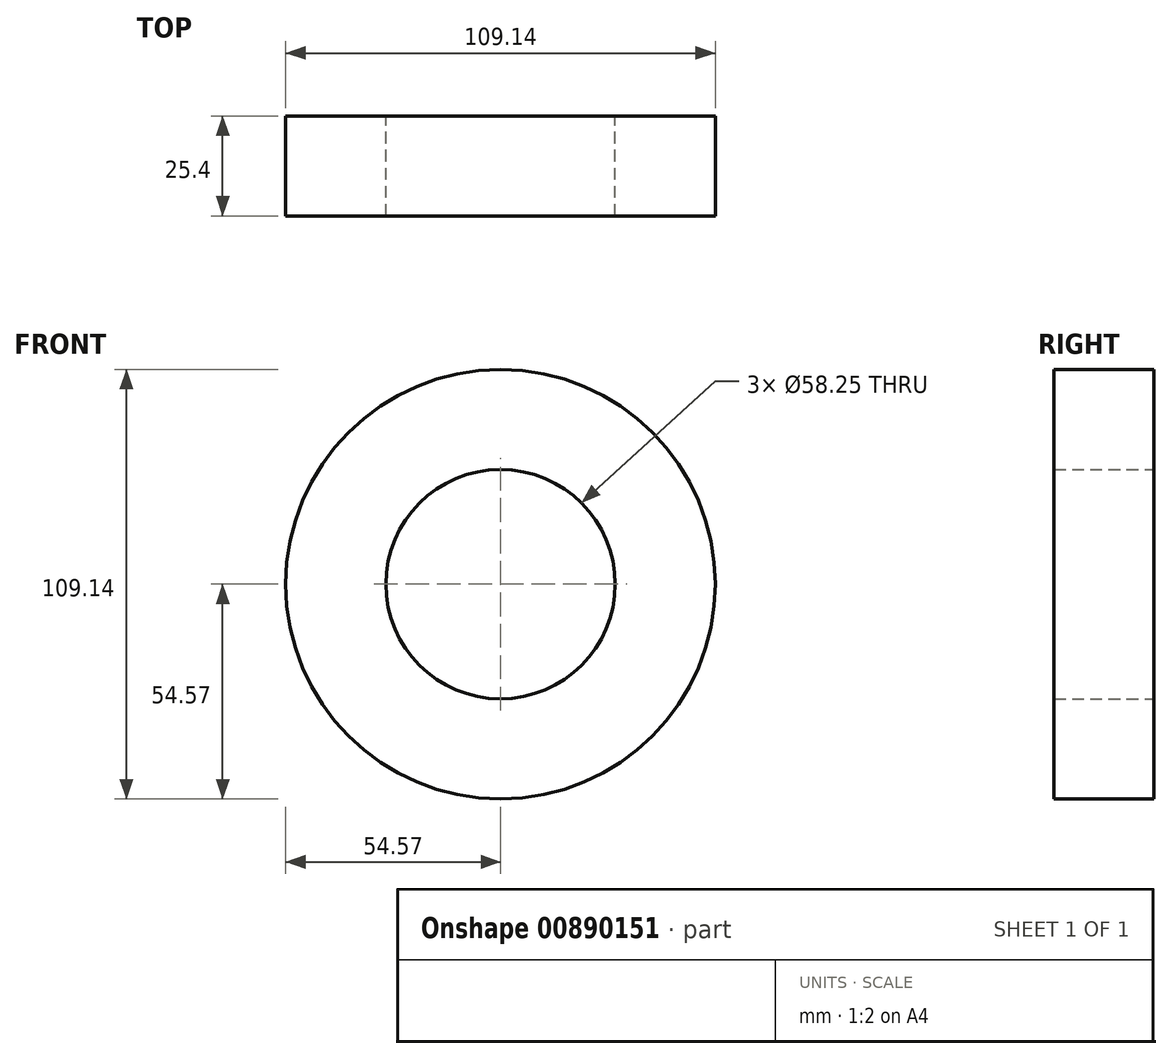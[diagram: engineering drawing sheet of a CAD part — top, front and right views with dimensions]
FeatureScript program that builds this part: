
annotation { "Feature Type Name" : "Feature", "Feature Type Description" : "" }
export const myFeature = defineFeature(function(context is Context, id is Id, definition is map)
    precondition{}
    {
        {
            var Q0;
            Q0=qCreatedBy(makeId("Front.planeOp"),FACE);
            var sketch = newSketch(context, id + "F0", { "sketchPlane" : qUnion([Q0])});
            skCircle(sketch, "E0", {"center": v(0, 0) * mm, "radius": 29.12 * mm});
            skSolve(sketch);
        }
        {
            var Q0;
            Q0=makeQuery(id+"F0.imprint","IMPRINT",FACE,{"disambiguationData":[TD([[makeQuery(id+"F0.imprint","IMPRINT",EDGE,{"derivedFrom":sQuery(id+"F0.wireOp",EDGE,"E0")}),1.0]])]});
            var sketch = newSketch(context, id + "F1", { "sketchPlane" : qUnion([Q0])});
            skCircle(sketch, "E1", {"center": v(0, 0) * mm, "radius": 54.57 * mm});
            skSolve(sketch);
        }
        {
            var Q0;
            Q0=makeQuery(id+"F1.imprint","IMPRINT",FACE,{"disambiguationData":[TD([[makeQuery(id+"F1.imprint","IMPRINT",EDGE,{"derivedFrom":sQuery(id+"F1.wireOp",EDGE,"E1")}),1.0]])]});
            extrude(context, id + "F2", {"entities" : qUnion([Q0]), "depth" : 25.4 * mm, "offsetDistance" : 25.4 * mm});
        }
    });
